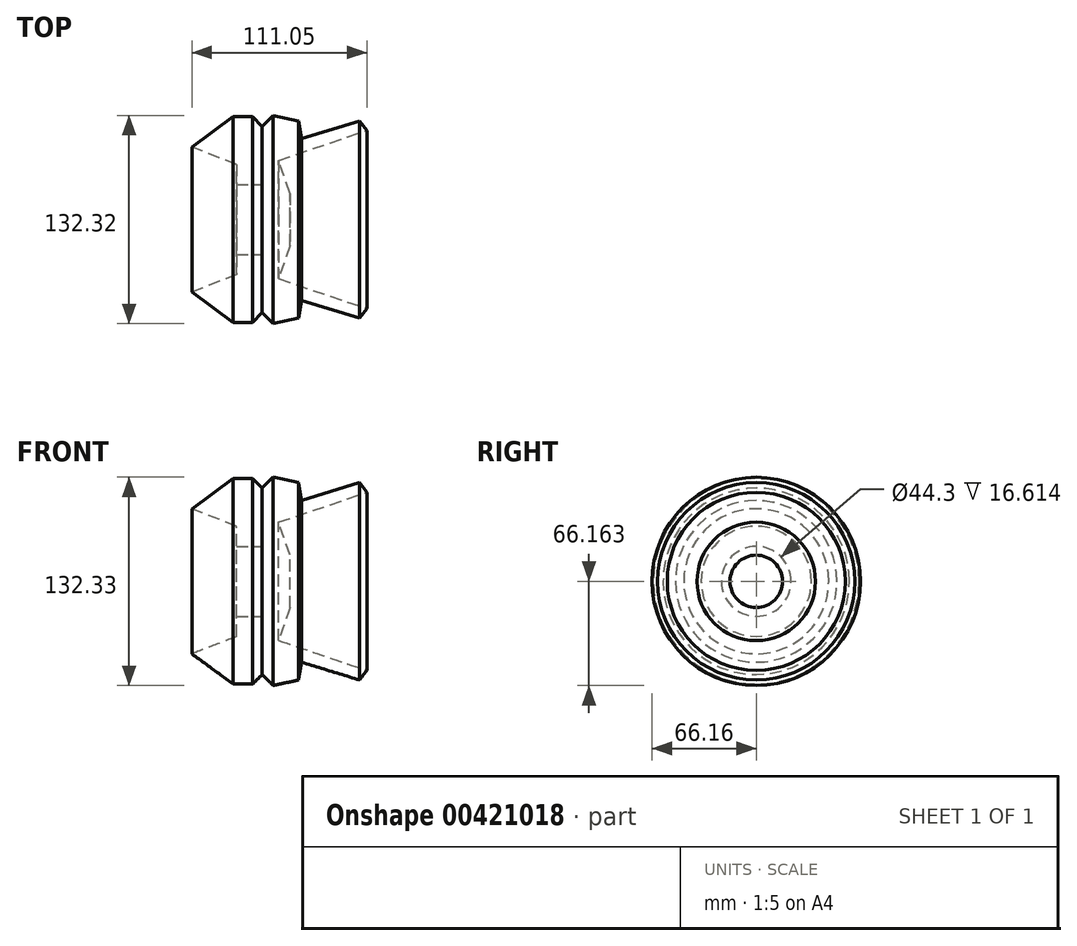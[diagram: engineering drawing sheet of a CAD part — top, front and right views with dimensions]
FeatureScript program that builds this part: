
annotation { "Feature Type Name" : "Feature", "Feature Type Description" : "" }
export const myFeature = defineFeature(function(context is Context, id is Id, definition is map)
    precondition{}
    {
        {
            var Q0;
            Q0=qCreatedBy(makeId("Front.planeOp"),FACE);
            var sketch = newSketch(context, id + "F0", { "sketchPlane" : qUnion([Q0])});
            skLineSegment(sketch, "E0", {"start": v(-32.94, 54.94) * mm, "end": v(-20.7, 54.94) * mm});
            skLineSegment(sketch, "E1", {"start": v(-20.7, 54.94) * mm, "end": v(-14.57, 48.82) * mm});
            skLineSegment(sketch, "E2", {"start": v(-14.57, 48.82) * mm, "end": v(-7.58, 55.82) * mm});
            skLineSegment(sketch, "E3", {"start": v(-7.58, 55.82) * mm, "end": v(8.45, 52.32) * mm});
            skLineSegment(sketch, "E4", {"start": v(8.45, 52.32) * mm, "end": v(10.5, 40.95) * mm});
            skLineSegment(sketch, "E5", {"start": v(10.5, 40.95) * mm, "end": v(47.22, 52.32) * mm});
            skLineSegment(sketch, "E6", {"start": v(47.22, 52.32) * mm, "end": v(51.88, 46.2) * mm});
            skLineSegment(sketch, "E7", {"start": v(51.88, 46.2) * mm, "end": v(-4.08, 27.25) * mm});
            skLineSegment(sketch, "E8", {"start": v(-4.08, 27.25) * mm, "end": v(3.01, 6.3) * mm});
            skLineSegment(sketch, "E9", {"start": v(3.01, 6.3) * mm, "end": v(3.01, -10.35) * mm});
            skLineSegment(sketch, "E10", {"start": v(3.01, -10.35) * mm, "end": v(-14.28, -10.35) * mm});
            skLineSegment(sketch, "E11", {"start": v(-14.28, -10.35) * mm, "end": v(-14.28, 11.8) * mm});
            skLineSegment(sketch, "E12", {"start": v(-14.28, 11.8) * mm, "end": v(-30.9, 11.8) * mm});
            skLineSegment(sketch, "E13", {"start": v(-30.9, 11.8) * mm, "end": v(-30.9, 24.63) * mm});
            skLineSegment(sketch, "E14", {"start": v(-30.9, 24.63) * mm, "end": v(-59.17, 35.7) * mm});
            skLineSegment(sketch, "E15", {"start": v(-59.17, 35.7) * mm, "end": v(-32.94, 54.94) * mm});
            skSolve(sketch);
        }
        {
            var Q0;
            Q0=makeQuery(id+"F0.imprint","IMPRINT",FACE,{"disambiguationData":[TD([[makeQuery(id+"F0.imprint","IMPRINT",EDGE,{"derivedFrom":sQuery(id+"F0.wireOp",EDGE,"E0")}),-1.0]])]});
            var Q1;
            Q1=sQuery(id+"F0.wireOp",EDGE,"E10");
            revolve(context, id + "F1", {"entities" : qUnion([Q0]), "axis" : qUnion([Q1]), "revolveType" : RevolveType.FULL});
        }
    });
